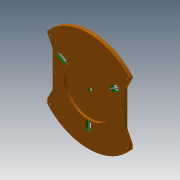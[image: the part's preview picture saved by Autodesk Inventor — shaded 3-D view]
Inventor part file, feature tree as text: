
AUTODESK INVENTOR PART (.ipt)
format: ipt  version: 2013 (Build 170138000, 138)  size: 551,936 bytes
history: native  units: mm
features: extrude x21, sketch x21
ambient origin geometry x8: Origin, YZ Plane, XZ Plane, XY Plane, X Axis, Y Axis, Z Axis, Center Point
bodies: Solid1 (feature_tree)
feature tree (42):
  extrude  "Extrusion1"  Depth=4.0mm
  extrude  "Extrusion2"  Depth=4.0mm
  extrude  "Extrusion3"  Depth=4.0mm
  extrude  "Extrusion4"  Depth=4.0mm
  extrude  "Extrusion5"  Depth=4.0mm
  extrude  "Extrusion6"  Depth=4.0mm
  extrude  "Extrusion7"  Depth=4.0mm
  sketch  "Sketch8"  dims[d14=4.0mm d15=4.0mm]
  sketch  "Sketch9"  dims[d16=4.0mm d17=4.0mm]
  sketch  "Sketch10"  dims[d18=4.0mm d19=4.0mm]
  extrude  "Extrusion8"  Depth=4.0mm
  extrude  "Extrusion9"  Depth=4.0mm
  extrude  "Extrusion10"  Depth=4.0mm
  extrude  "Extrusion11"  Depth=4.0mm
  extrude  "Extrusion12"  Depth=4.0mm
  extrude  "Extrusion13"  Depth=2.0mm TaperAngle=0.0deg
  extrude  "Extrusion14"  Depth=8.0mm TaperAngle=0.0deg
  extrude  "Extrusion15"  Depth=10.0mm TaperAngle=0.0deg
  extrude  "Extrusion16"  Depth=8.0mm
  sketch  "Sketch18"  dims[d41=11.3mm d42=0.0mm d43=11.3mm d44=0.0mm]
  extrude  "Extrusion17"  Depth=11.3mm TaperAngle=0.0deg
  extrude  "Extrusion18"  Depth=11.3mm TaperAngle=0.0deg
  extrude  "Extrusion19"  Depth=100.0mm
  extrude  "Extrusion20"  Depth=6.0mm
  extrude  "Extrusion21"  Depth=3.0mm
  sketch  "Sketch1"  dims[d0=4.0mm d1=4.0mm]
  sketch  "Sketch2"  dims[d2=4.0mm d3=4.0mm]
  sketch  "Sketch3"  dims[d4=4.0mm d5=4.0mm]
  sketch  "Sketch4"  dims[d6=4.0mm d7=4.0mm]
  sketch  "Sketch5"  dims[d8=4.0mm d9=4.0mm]
  sketch  "Sketch6"  dims[d10=4.0mm d11=4.0mm]
  sketch  "Sketch7"  dims[d12=4.0mm d13=4.0mm]
  sketch  "Sketch11"  dims[d20=4.0mm d21=4.0mm]
  sketch  "Sketch12"  dims[d22=4.0mm d23=4.0mm]
  sketch  "Sketch13"  dims[d24=4.0mm d25=2.0mm d26=0.0mm]
  sketch  "Sketch14"  dims[d27=1.3mm d28=0.0mm d29=8.0mm d30=0.0mm]
  sketch  "Sketch15"  dims[d31=10.0mm d32=0.0mm d33=10.0mm d34=0.0mm]
  sketch  "Sketch16"  dims[d35=3.0mm d36=8.0mm]
  sketch  "Sketch17"  dims[d37=11.3mm d38=0.0mm d39=11.3mm d40=0.0mm]
  sketch  "Sketch19"  dims[d45=100.0mm d46=100.0mm]
  sketch  "Sketch20"  dims[d47=11.3mm d48=0.0mm d49=6.0mm]
  sketch  "Sketch21"  dims[d50=11.3mm d51=0.0mm d52=3.0mm d53=3.0mm d54=11.3mm d55=0.0mm d56=11.3mm d57=0.0mm d58=1.3mm d59=0.0mm d60=120.0mm d63=60.191mm d65=37.2mm d66=14.209mm d67=91.5mm d68=8.0mm d69=0.0mm d70=3.8mm d71=0.0mm d72=10.0mm d73=20.0mm d74=10.0mm d75=14.0mm d87=20.0mm d88=10.0mm d89=20.0mm d90=10.0mm d91=14.0mm d92=10.0mm d93=14.0mm d94=10.0mm d95=10.0mm d96=0.0mm d97=30.0deg d98=2.5mm d99=2.5mm d100=2.5mm d101=2.5mm d102=2.5mm d103=2.5mm d104=2.5mm d105=0.0mm d106=20.0mm d107=0.0mm d108=20.0mm d109=0.0mm d110=20.0mm d111=0.0mm]
